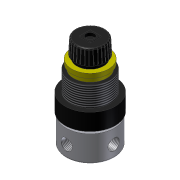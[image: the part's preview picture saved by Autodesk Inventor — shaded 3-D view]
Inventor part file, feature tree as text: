
AUTODESK INVENTOR PART (.ipt)
format: ipt  version: unknown  size: 717,312 bytes
history: native  units: mm (DEFAULTED — no unit token found)
features: extrude x12, sketch x12, projected_geometry x7, fillet x3, pattern_circular x2, thread x2, plane x1
ambient origin geometry x8: Origin, YZ Plane, XZ Plane, XY Plane, X Axis, Y Axis, Z Axis, Center Point
feature tree (39):
  extrude  "Extrusion1"  Depth=19.5mm TaperAngle=0.0deg
  extrude  "Extrusion2"  Depth=37.5mm
  extrude  "Extrusion3"  Depth=30.0mm
  extrude  "Extrusion4"  Depth=25.0mm
  extrude  "Extrusion5"  Depth=27.5mm
  extrude  "Extrusion6"  Depth=20.0mm
  extrude  "Extrusion7"  Depth=23.0mm
  extrude  "Extrusion8"  Depth=1.0mm
  fillet  "Fillet1"  Radius=0.5mm
  extrude  "Extrusion9"  Depth=300.0mm TaperAngle=360.0deg
  fillet  "Fillet2"  Radius=10.0mm
  pattern_circular  "Circular Pattern1"  Count=4 Angle=360.0deg
  thread  "Thread1"  [1 undecoded]
  plane  "Work Plane1"
  extrude  "Extrusion10"  Depth=2.0mm TaperAngle=0.0deg
  thread  "Thread2"  [1 undecoded]
  pattern_circular  "Circular Pattern2"  [2 undecoded]
  fillet  "Fillet3"  [1 undecoded]
  extrude  "Extrusion11"  [1 undecoded]
  extrude  "Extrusion12"  [1 undecoded]
  sketch  "Sketch1"  dims[d0=36.0mm d1=19.5mm d2=0.0mm]
  sketch  "Sketch2"  dims[d3=2.0mm d4=0.0mm d5=37.5mm]
  sketch  "Sketch3"  dims[d6=12.5mm d7=0.0mm d8=30.0mm]
  projected_geometry  "Projected Loop1"
  sketch  "Sketch4"  dims[d9=15.0mm d10=0.0mm d11=25.0mm]
  sketch  "Sketch5"  dims[d12=3.3mm d13=0.0mm d14=27.5mm]
  projected_geometry  "Projected Loop2"
  sketch  "Sketch6"  dims[d15=3.3mm d16=0.0mm d17=20.0mm]
  projected_geometry  "Projected Loop3"
  sketch  "Sketch7"  dims[d18=3.0mm d19=0.0mm d20=23.0mm]
  projected_geometry  "Projected Loop4"
  sketch  "Sketch8"  dims[d21=11.0mm d22=-0.523599mm d23=1.0mm d24=0.5mm d25=0.0mm]
  projected_geometry  "Projected Loop5"
  sketch  "Sketch9"  dims[d26=0.15mm d27=300.0mm d29=360.0deg d30=10.0mm d31=0.0mm]
  sketch  "Sketch10"  dims[d32=9.75mm d33=0.0mm]
  projected_geometry  "Projected Loop6"
  sketch  "Sketch11"  dims[d34=10.0mm d35=0.0mm d36=8.5mm d37=40.0mm d39=360.0deg d40=1.0mm]
  sketch  "Sketch12"  dims[d41=6.3mm d42=2.0mm d43=0.0mm d44=0.5mm d45=0.0mm]
  projected_geometry  "Projected Loop7"
note: 7 required parameter values undecoded (feature->parameter linkage not recoverable at this tier; creation-order binding heuristic only, values carry confidence <= 0.55)
